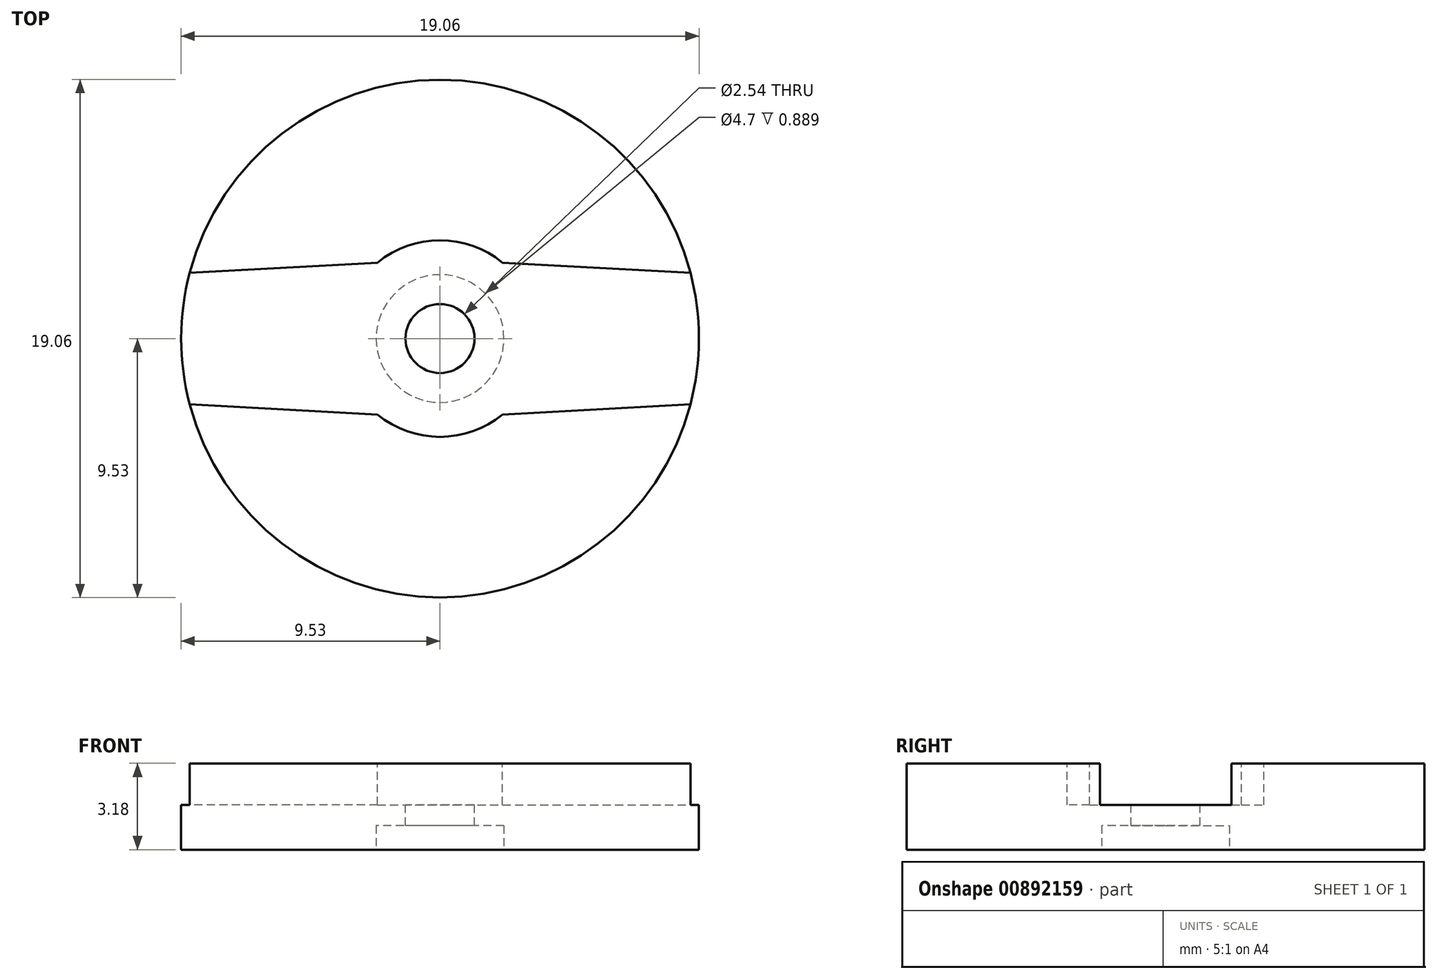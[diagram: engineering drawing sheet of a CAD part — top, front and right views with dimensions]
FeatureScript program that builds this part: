
annotation { "Feature Type Name" : "Feature", "Feature Type Description" : "" }
export const myFeature = defineFeature(function(context is Context, id is Id, definition is map)
    precondition{}
    {
        {
            var Q0;
            Q0=qCreatedBy(makeId("Top.planeOp"),FACE);
            var sketch = newSketch(context, id + "F0", { "sketchPlane" : qUnion([Q0])});
            skCircle(sketch, "E0", {"center": v(0, 0) * mm, "radius": 9.53 * mm});
            skSolve(sketch);
        }
        {
            var Q0;
            Q0 = qSketchRegion(id + "F0", true);
            extrude(context, id + "F1", {"entities" : qUnion([Q0]), "depth" : 3.17 * mm, "offsetDistance" : 25.4 * mm});
        }
        {
            var Q0;
            Q0=makeQuery(id+"F1.opExtrude","CAP_FACE",FACE,{"disambiguationData":[OSD([sQuery(id+"F0.wireOp",EDGE,"E0")])],"isStart":false});
            var sketch = newSketch(context, id + "F2", { "sketchPlane" : qUnion([Q0])});
            skArc(sketch, "E1", {"start": v(14.08, -2.16) * mm, "mid": v(16.13, 0) * mm, "end": v(14.08, 2.16) * mm});
            skLineSegment(sketch, "E2", {"start": v(14.08, 2.16) * mm, "end": v(2.3, 2.8) * mm});
            skLineSegment(sketch, "E3", {"start": v(2.3, 2.8) * mm, "end": v(2.3, -2.8) * mm, "construction": true});
            skLineSegment(sketch, "E4", {"start": v(2.3, -2.8) * mm, "end": v(14.08, -2.16) * mm});
            skLineSegment(sketch, "E5", {"start": v(0, -8.97) * mm, "end": v(0, 12.55) * mm, "construction": true});
            skLineSegment(sketch, "E6.MirrorCS", {"start": v(-2.3, -2.8) * mm, "end": v(-14.08, -2.16) * mm});
            skArc(sketch, "E7.MirrorCS", {"start": v(-14.08, -2.16) * mm, "mid": v(-16.13, 0) * mm, "end": v(-14.08, 2.16) * mm});
            skLineSegment(sketch, "E8.MirrorCS", {"start": v(-14.08, 2.16) * mm, "end": v(-2.3, 2.8) * mm});
            skLineSegment(sketch, "E9.MirrorCS", {"start": v(-2.3, 2.8) * mm, "end": v(-2.3, -2.8) * mm, "construction": true});
            skPoint(sketch, "E10", {"position": v(-16.13, 0) * mm});
            skPoint(sketch, "E11", {"position": v(16.13, 0) * mm});
            skArc(sketch, "E12.0", {"start": v(2.3, 2.8) * mm, "mid": v(0, 3.62) * mm, "end": v(-2.3, 2.8) * mm});
            skArc(sketch, "E13.trimOffspring", {"start": v(-2.3, -2.8) * mm, "mid": v(0, -3.62) * mm, "end": v(2.3, -2.8) * mm});
            skSolve(sketch);
        }
        {
            var Q0;
            Q0 = qSketchRegion(id + "F2", true);
            extrude(context, id + "F3", {"entities" : qUnion([Q0]), "operationType" : NewBodyOperationType.REMOVE, "oppositeDirection" : true, "depth" : 1.52 * mm, "offsetDistance" : 25.4 * mm});
        }
        {
            var Q0;
            Q0=makeQuery(id+"F3.boolean.opBoolean","COPY",FACE,{"derivedFrom":makeQuery(id+"F3.opExtrude","CAP_FACE",FACE,{"disambiguationData":[OSD([sQuery(id+"F2.wireOp",EDGE,"E1"),sQuery(id+"F2.wireOp",EDGE,"E2"),sQuery(id+"F2.wireOp",EDGE,"E4"),sQuery(id+"F2.wireOp",EDGE,"E6.MirrorCS"),sQuery(id+"F2.wireOp",EDGE,"E7.MirrorCS"),sQuery(id+"F2.wireOp",EDGE,"E8.MirrorCS"),sQuery(id+"F2.wireOp",EDGE,"E12.0"),sQuery(id+"F2.wireOp",EDGE,"E13.trimOffspring")])],"isStart":false})});
            var sketch = newSketch(context, id + "F4", { "sketchPlane" : qUnion([Q0])});
            skCircle(sketch, "E14", {"center": v(0, 0) * mm, "radius": 1.27 * mm});
            skSolve(sketch);
        }
        {
            var Q0;
            Q0 = qSketchRegion(id + "F4", true);
            extrude(context, id + "F5", {"entities" : qUnion([Q0]), "operationType" : NewBodyOperationType.REMOVE, "oppositeDirection" : true, "depth" : 25.4 * mm, "offsetDistance" : 25.4 * mm});
        }
        {
            var Q0;
            Q0=makeQuery(id+"F1.opExtrude","CAP_FACE",FACE,{"disambiguationData":[OSD([sQuery(id+"F0.wireOp",EDGE,"E0")])],"isStart":true});
            var sketch = newSketch(context, id + "F6", { "sketchPlane" : qUnion([Q0])});
            skCircle(sketch, "E15", {"center": v(0, 0) * mm, "radius": 2.35 * mm});
            skSolve(sketch);
        }
        {
            var Q0;
            Q0 = qSketchRegion(id + "F6", true);
            var Q1;
            Q1=makeQuery(id+"F3.boolean.opBoolean","COPY",FACE,{"derivedFrom":makeQuery(id+"F3.opExtrude","CAP_FACE",FACE,{"disambiguationData":[OSD([sQuery(id+"F2.wireOp",EDGE,"E1"),sQuery(id+"F2.wireOp",EDGE,"E2"),sQuery(id+"F2.wireOp",EDGE,"E4"),sQuery(id+"F2.wireOp",EDGE,"E6.MirrorCS"),sQuery(id+"F2.wireOp",EDGE,"E7.MirrorCS"),sQuery(id+"F2.wireOp",EDGE,"E8.MirrorCS"),sQuery(id+"F2.wireOp",EDGE,"E12.0"),sQuery(id+"F2.wireOp",EDGE,"E13.trimOffspring")])],"isStart":false})});
            extrude(context, id + "F7", {"entities" : qUnion([Q0]), "operationType" : NewBodyOperationType.REMOVE, "endBound" : BoundingType.UP_TO_SURFACE, "oppositeDirection" : true, "depth" : 1.02 * mm, "endBoundEntityFace" : qUnion([Q1]), "hasOffset" : true, "offsetDistance" : 0.76 * mm});
        }
    });
